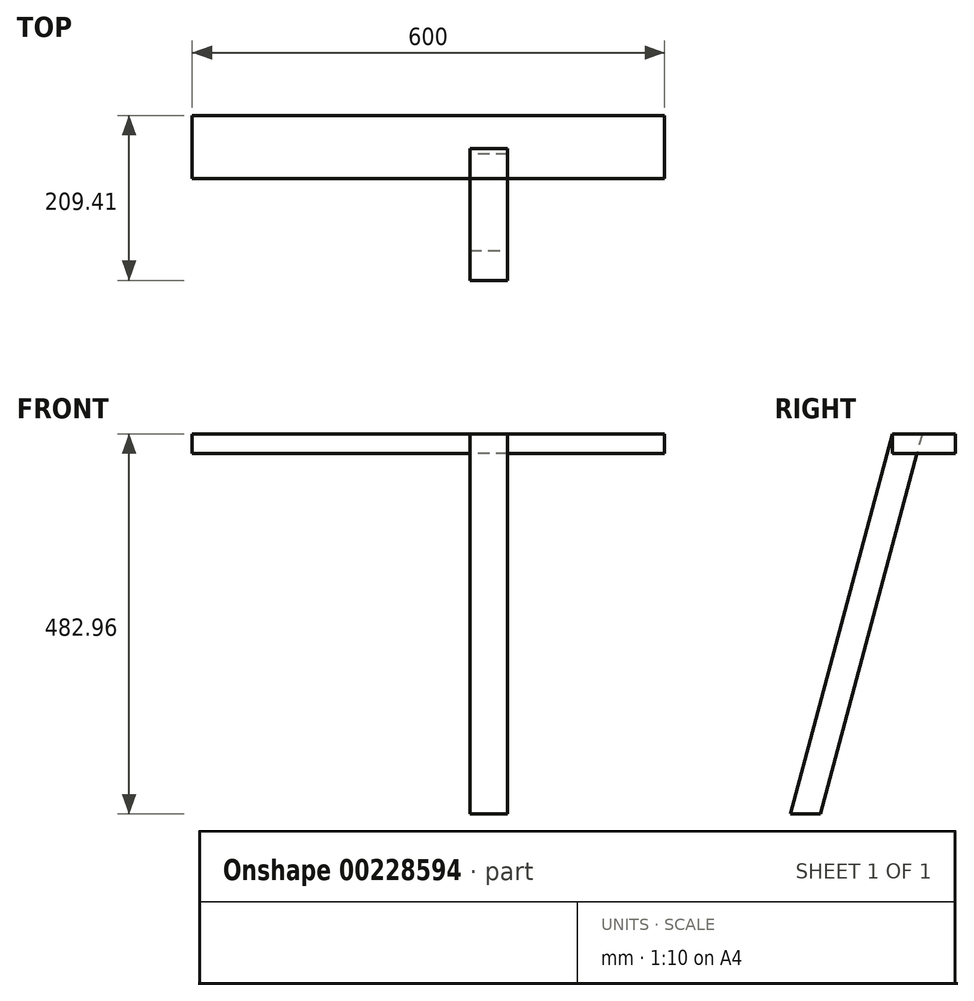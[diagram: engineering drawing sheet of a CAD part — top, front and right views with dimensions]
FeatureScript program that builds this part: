
annotation { "Feature Type Name" : "Feature", "Feature Type Description" : "" }
export const myFeature = defineFeature(function(context is Context, id is Id, definition is map)
    precondition{}
    {
        {
            var Q0;
            Q0=qCreatedBy(makeId("Top.planeOp"),FACE);
            var sketch = newSketch(context, id + "F0", { "sketchPlane" : qUnion([Q0])});
            skLineSegment(sketch, "E0.bottom", {"start": v(-246.53, -119.2) * mm, "end": v(353.47, -119.2) * mm});
            skLineSegment(sketch, "E0.top", {"start": v(-246.53, -39.2) * mm, "end": v(353.47, -39.2) * mm});
            skLineSegment(sketch, "E0.left", {"start": v(-246.53, -119.2) * mm, "end": v(-246.53, -39.2) * mm});
            skLineSegment(sketch, "E0.right", {"start": v(353.47, -119.2) * mm, "end": v(353.47, -39.2) * mm});
            skSolve(sketch);
        }
        {
            var Q0;
            Q0=makeQuery(id+"F0.imprint","IMPRINT",FACE,{"disambiguationData":[TD([[makeQuery(id+"F0.imprint","IMPRINT",EDGE,{"derivedFrom":sQuery(id+"F0.wireOp",EDGE,"E0.bottom")}),1.0]])]});
            extrude(context, id + "F1", {"entities" : qUnion([Q0]), "depth" : 25 * mm});
        }
        {
            var Q0;
            Q0=makeQuery(id+"F1.opExtrude","CAP_FACE",FACE,{"disambiguationData":[OSD([sQuery(id+"F0.wireOp",EDGE,"E0.bottom"),sQuery(id+"F0.wireOp",EDGE,"E0.top"),sQuery(id+"F0.wireOp",EDGE,"E0.left"),sQuery(id+"F0.wireOp",EDGE,"E0.right")])],"isStart":false});
            var sketch = newSketch(context, id + "F2", { "sketchPlane" : qUnion([Q0])});
            skLineSegment(sketch, "E1.bottom", {"start": v(106.35, -119.2) * mm, "end": v(154.35, -119.2) * mm});
            skLineSegment(sketch, "E1.top", {"start": v(106.35, -81.2) * mm, "end": v(154.35, -81.2) * mm});
            skLineSegment(sketch, "E1.left", {"start": v(106.35, -119.2) * mm, "end": v(106.35, -81.2) * mm});
            skLineSegment(sketch, "E1.right", {"start": v(154.35, -119.2) * mm, "end": v(154.35, -81.2) * mm});
            skSolve(sketch);
        }
        {
            var Q0;
            Q0=sQuery(id+"F2.wireOp",VERTEX,"E1.bottom.start");
            var Q1;
            Q1=sQuery(id+"F2.wireOp",EDGE,"E1.top");
            cPlane(context, id + "F3", {"entities" : qUnion([Q0, Q1]), "cplaneType" : CPlaneType.LINE_POINT, "offset" : 25 * mm, "width" : 150 * mm, "height" : 150 * mm});
        }
        {
            var Q0;
            Q0=qCreatedBy(id+"F3.planeOp",FACE);
            var sketch = newSketch(context, id + "F6", { "sketchPlane" : qUnion([Q0])});
            skLineSegment(sketch, "E2", {"start": v(-119.2, 25) * mm, "end": v(-248.6, -457.96) * mm});
            skLineSegment(sketch, "E3", {"start": v(-248.6, -457.96) * mm, "end": v(-119.2, 25) * mm, "construction": true});
            skLineSegment(sketch, "E4", {"start": v(-119.2, 25) * mm, "end": v(-119.2, 0) * mm, "construction": true});
            skSolve(sketch);
        }
        {
            var Q0;
            Q0=makeQuery(id+"F2.imprint","IMPRINT",FACE,{"disambiguationData":[TD([[makeQuery(id+"F2.imprint","IMPRINT",EDGE,{"derivedFrom":sQuery(id+"F2.wireOp",EDGE,"E1.bottom")}),1.0]])]});
            var Q1;
            Q1=sQuery(id+"F6.wireOp",EDGE,"E2");
            sweep(context, id + "F4", {"profiles" : qUnion([Q0]), "path" : qUnion([Q1])});
        }
        {
            var Q0;
            Q0=makeQuery(id+"F4.opSweep","SWEPT_BODY",BODY,{"disambiguationData":[OSD([sQuery(id+"F2.wireOp",EDGE,"E1.bottom"),sQuery(id+"F2.wireOp",EDGE,"E1.top"),sQuery(id+"F2.wireOp",EDGE,"E1.left"),sQuery(id+"F2.wireOp",EDGE,"E1.right"),sQuery(id+"F6.wireOp",EDGE,"E2")])]});
            var Q1;
            Q1=makeQuery(id+"F1.opExtrude","SWEPT_BODY",BODY,{"disambiguationData":[OSD([sQuery(id+"F0.wireOp",EDGE,"E0.bottom"),sQuery(id+"F0.wireOp",EDGE,"E0.top"),sQuery(id+"F0.wireOp",EDGE,"E0.left"),sQuery(id+"F0.wireOp",EDGE,"E0.right")])]});
            booleanBodies(context, id + "F5", {"operationType" : BooleanOperationType.SUBTRACTION, "tools" : qUnion([Q0]), "targets" : qUnion([Q1]), "keepTools" : true});
        }
    });
